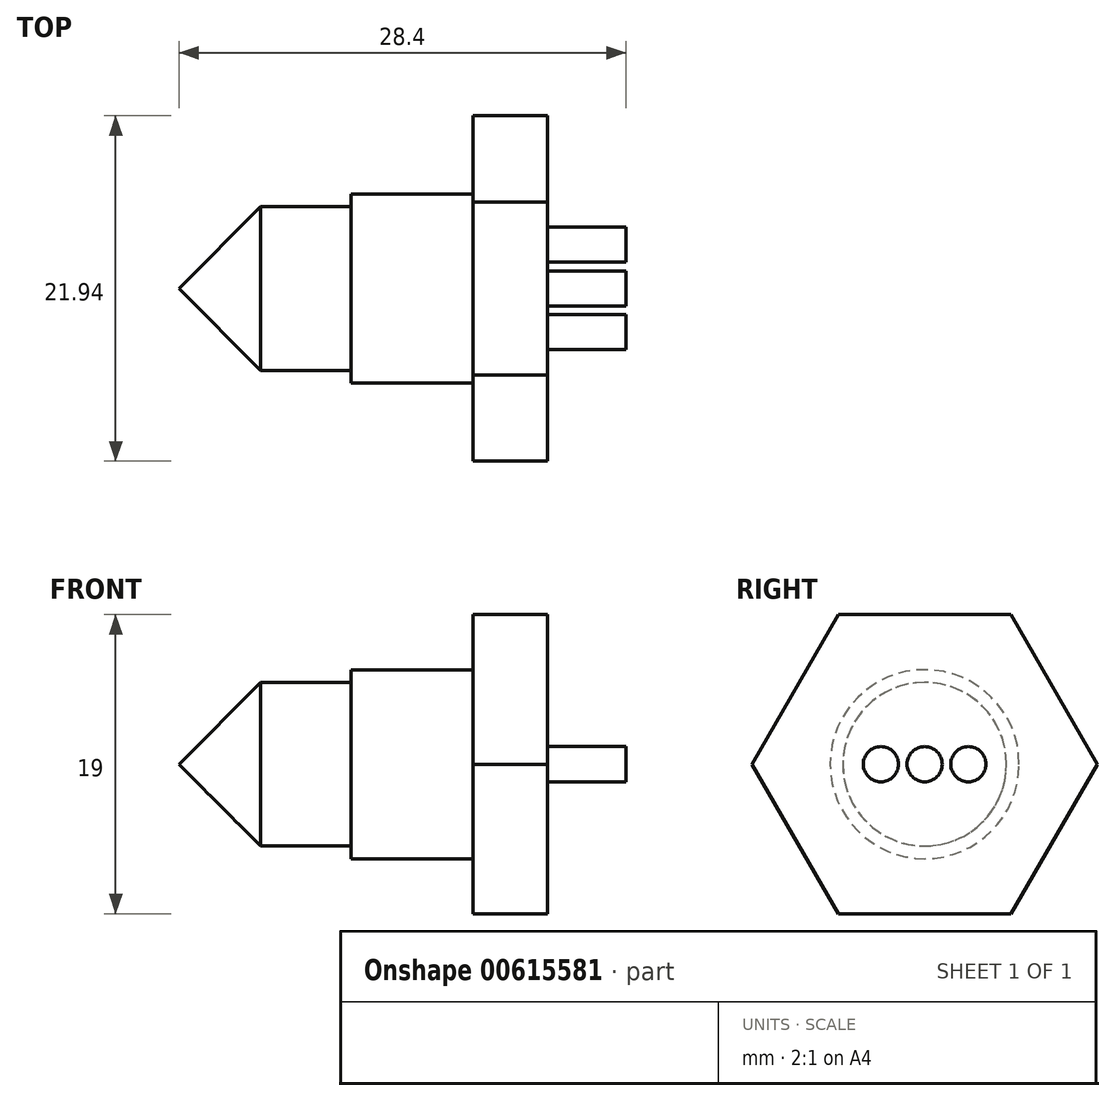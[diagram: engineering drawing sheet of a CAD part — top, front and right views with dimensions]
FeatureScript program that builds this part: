
annotation { "Feature Type Name" : "Feature", "Feature Type Description" : "" }
export const myFeature = defineFeature(function(context is Context, id is Id, definition is map)
    precondition{}
    {
        {
            var Q0;
            Q0=qCreatedBy(makeId("Front.planeOp"),FACE);
            var sketch = newSketch(context, id + "F0", { "sketchPlane" : qUnion([Q0])});
            skLineSegment(sketch, "E0", {"start": v(0, 6) * mm, "end": v(0, 0) * mm});
            skLineSegment(sketch, "E1", {"start": v(0, 6) * mm, "end": v(-7.75, 6) * mm});
            skLineSegment(sketch, "E2", {"start": v(-7.75, 6) * mm, "end": v(-7.75, 5.2) * mm});
            skLineSegment(sketch, "E3", {"start": v(-7.75, 5.2) * mm, "end": v(-13.5, 5.2) * mm});
            skLineSegment(sketch, "E4", {"start": v(-13.5, 5.2) * mm, "end": v(-18.7, 0) * mm});
            skLineSegment(sketch, "E5", {"start": v(-18.7, 0) * mm, "end": v(0, 0) * mm});
            skSolve(sketch);
        }
        {
            var Q0;
            Q0 = qSketchRegion(id + "F0", true);
            var Q1;
            Q1=sQuery(id+"F0.wireOp",EDGE,"E5");
            revolve(context, id + "F1", {"entities" : qUnion([Q0]), "axis" : qUnion([Q1]), "revolveType" : RevolveType.FULL});
        }
        {
            var Q0;
            Q0=makeQuery(id+"F1.opRevolve","SWEPT_FACE",FACE,{"disambiguationData":[OSD([sQuery(id+"F0.wireOp",EDGE,"E0")])]});
            var sketch = newSketch(context, id + "F2", { "sketchPlane" : qUnion([Q0])});
            skCircle(sketch, "E6.cCircle", {"center": v(0, 0) * mm, "radius": 9.5 * mm, "construction": true});
            skLineSegment(sketch, "E6.0", {"start": v(5.48, -9.5) * mm, "end": v(-5.48, -9.5) * mm});
            skLineSegment(sketch, "E6.1", {"start": v(-5.48, -9.5) * mm, "end": v(-10.97, 0) * mm});
            skLineSegment(sketch, "E6.2", {"start": v(-10.97, 0) * mm, "end": v(-5.48, 9.5) * mm});
            skLineSegment(sketch, "E6.3", {"start": v(-5.48, 9.5) * mm, "end": v(5.48, 9.5) * mm});
            skLineSegment(sketch, "E6.4", {"start": v(5.48, 9.5) * mm, "end": v(10.97, 0) * mm});
            skLineSegment(sketch, "E6.5", {"start": v(10.97, 0) * mm, "end": v(5.48, -9.5) * mm});
            skPoint(sketch, "E6.0.midPoint", {"position": v(0, -9.5) * mm});
            skSolve(sketch);
        }
        {
            var Q0;
            Q0 = qSketchRegion(id + "F2", true);
            extrude(context, id + "F3", {"entities" : qUnion([Q0]), "operationType" : NewBodyOperationType.ADD, "depth" : 4.7 * mm, "offsetDistance" : 25 * mm});
        }
        {
            var Q0;
            Q0=makeQuery(id+"F3.opExtrude","CAP_FACE",FACE,{"disambiguationData":[OSD([sQuery(id+"F2.wireOp",EDGE,"E6.0"),sQuery(id+"F2.wireOp",EDGE,"E6.1"),sQuery(id+"F2.wireOp",EDGE,"E6.2"),sQuery(id+"F2.wireOp",EDGE,"E6.3"),sQuery(id+"F2.wireOp",EDGE,"E6.4"),sQuery(id+"F2.wireOp",EDGE,"E6.5")])],"isStart":false});
            var sketch = newSketch(context, id + "F4", { "sketchPlane" : qUnion([Q0])});
            skCircle(sketch, "E7", {"center": v(-2.78, 0) * mm, "radius": 1.12 * mm});
            skLineSegment(sketch, "E8", {"start": v(0, 0) * mm, "end": v(0, 3) * mm, "construction": true});
            skCircle(sketch, "E9.MirrorC", {"center": v(2.78, 0) * mm, "radius": 1.12 * mm});
            skCircle(sketch, "E10", {"center": v(0, 0) * mm, "radius": 1.12 * mm});
            skSolve(sketch);
        }
        {
            var Q0;
            Q0 = qSketchRegion(id + "F4", true);
            extrude(context, id + "F5", {"entities" : qUnion([Q0]), "operationType" : NewBodyOperationType.ADD, "depth" : 5 * mm, "offsetDistance" : 25 * mm});
        }
    });
